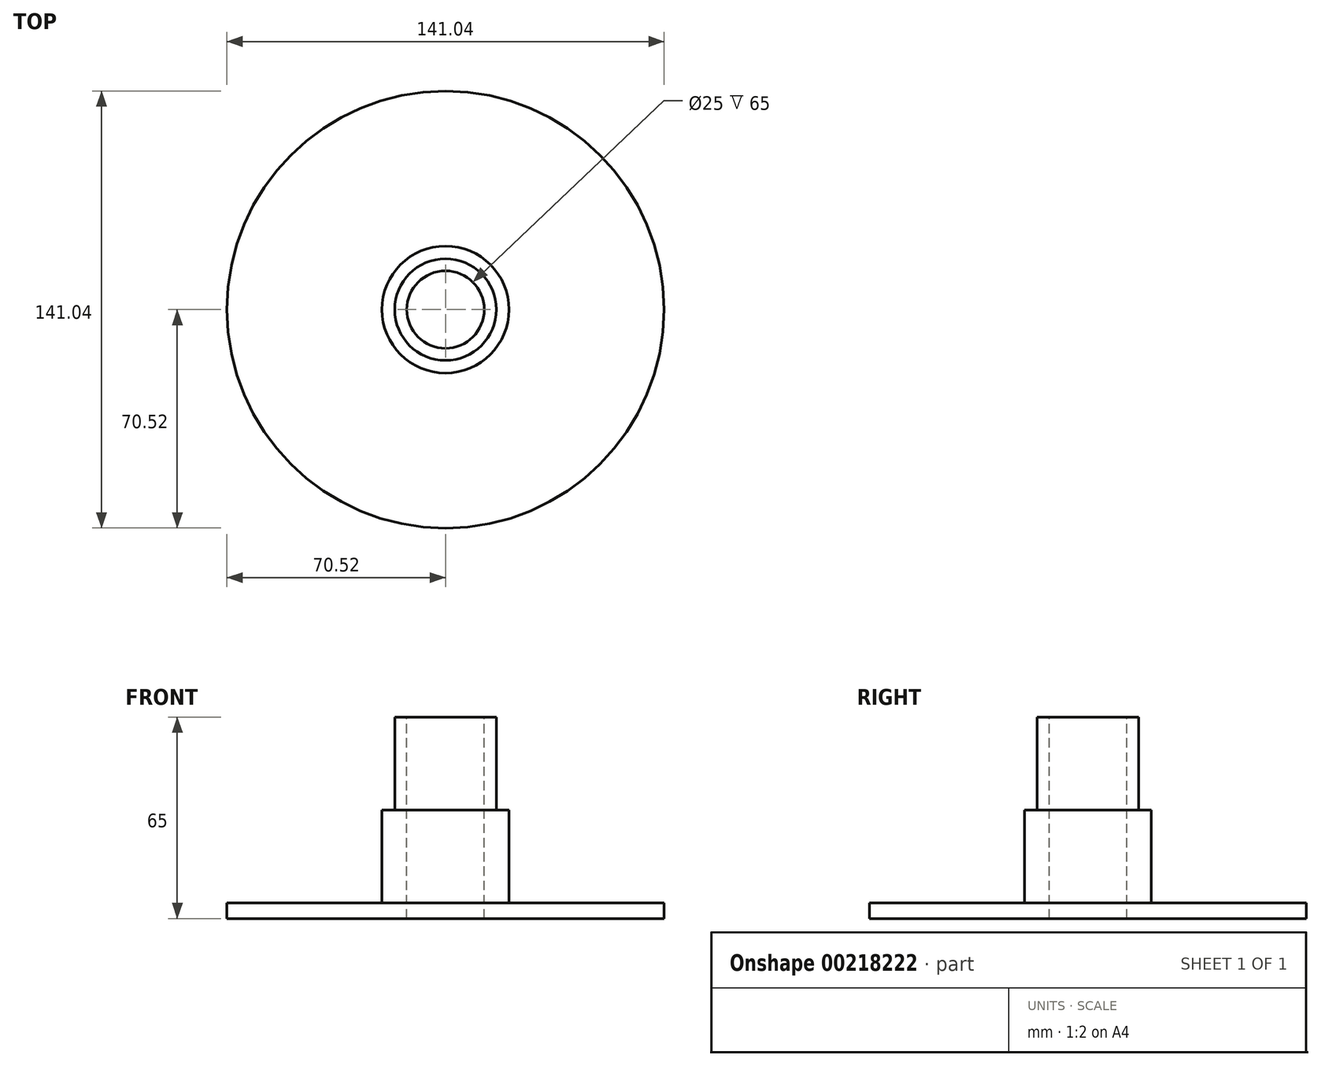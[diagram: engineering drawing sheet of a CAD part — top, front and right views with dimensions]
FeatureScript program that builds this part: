
annotation { "Feature Type Name" : "Feature", "Feature Type Description" : "" }
export const myFeature = defineFeature(function(context is Context, id is Id, definition is map)
    precondition{}
    {
        {
            var Q0;
            Q0=qCreatedBy(makeId("Front.planeOp"),FACE);
            var sketch = newSketch(context, id + "F0", { "sketchPlane" : qUnion([Q0])});
            skLineSegment(sketch, "E0.bottom", {"start": v(71.48, 6.77) * mm, "end": v(-70.52, 6.77) * mm});
            skLineSegment(sketch, "E0.top", {"start": v(71.48, 1.77) * mm, "end": v(-70.52, 1.77) * mm});
            skLineSegment(sketch, "E0.left", {"start": v(71.48, 6.77) * mm, "end": v(71.48, 1.77) * mm});
            skLineSegment(sketch, "E0.right", {"start": v(-70.52, 6.77) * mm, "end": v(-70.52, 1.77) * mm});
            skLineSegment(sketch, "E1.top", {"start": v(20.5, 66.77) * mm, "end": v(-20.5, 66.77) * mm});
            skLineSegment(sketch, "E1.left", {"start": v(20.5, 6.77) * mm, "end": v(20.5, 66.77) * mm});
            skLineSegment(sketch, "E1.right", {"start": v(-20.5, 6.77) * mm, "end": v(-20.5, 66.77) * mm});
            skPoint(sketch, "E1.middle", {"position": v(0, 36.77) * mm});
            skLineSegment(sketch, "E2", {"start": v(-12.5, 66.77) * mm, "end": v(-12.5, 6.77) * mm});
            skLineSegment(sketch, "E3.MirrorCS", {"start": v(12.5, 66.77) * mm, "end": v(12.5, 6.77) * mm});
            skLineSegment(sketch, "E4", {"start": v(-16.4, 66.77) * mm, "end": v(-16.4, 36.77) * mm});
            skLineSegment(sketch, "E5", {"start": v(-16.4, 36.77) * mm, "end": v(-20.5, 36.77) * mm});
            skLineSegment(sketch, "E6.MirrorCS", {"start": v(16.4, 36.77) * mm, "end": v(20.5, 36.77) * mm});
            skLineSegment(sketch, "E7.MirrorCS", {"start": v(16.4, 66.77) * mm, "end": v(16.4, 36.77) * mm});
            skLineSegment(sketch, "E8", {"start": v(-16.4, 36.77) * mm, "end": v(-12.5, 36.77) * mm});
            skLineSegment(sketch, "E9.MirrorCS", {"start": v(16.4, 36.77) * mm, "end": v(12.5, 36.77) * mm});
            skLineSegment(sketch, "E10", {"start": v(-12.5, 6.77) * mm, "end": v(-12.5, 1.77) * mm});
            skLineSegment(sketch, "E11.MirrorCS", {"start": v(12.5, 6.77) * mm, "end": v(12.5, 1.77) * mm});
            skLineSegment(sketch, "E12", {"start": v(0, 81.08) * mm, "end": v(0, -48.61) * mm, "construction": true});
            skSolve(sketch);
        }
        {
            var Q0;
            {var subQ0=sQuery(id+"F0.wireOp",EDGE,"E0.right");Q0=makeQuery(id+"F0.imprint","IMPRINT",FACE,{"disambiguationData":[TD([[makeQuery(id+"F0.imprint","IMPRINT",EDGE,{"derivedFrom":subQ0}),1.0]])]});}
            var Q1;
            {var subQ0=sQuery(id+"F0.wireOp",EDGE,"E5");Q1=makeQuery(id+"F0.imprint","IMPRINT",FACE,{"disambiguationData":[TD([[makeQuery(id+"F0.imprint","IMPRINT",EDGE,{"derivedFrom":subQ0}),1.0]])]});}
            var Q2;
            {var subQ3=sQuery(id+"F0.wireOp",EDGE,"E4");Q2=makeQuery(id+"F0.imprint","IMPRINT",FACE,{"disambiguationData":[TD([[makeQuery(id+"F0.imprint","IMPRINT",EDGE,{"derivedFrom":subQ3}),1.0]])]});}
            var Q3;
            Q3=sQuery(id+"F0.wireOp",EDGE,"E12");
            revolve(context, id + "F1", {"entities" : qUnion([Q0, Q1, Q2]), "axis" : qUnion([Q3]), "revolveType" : RevolveType.FULL});
        }
    });
